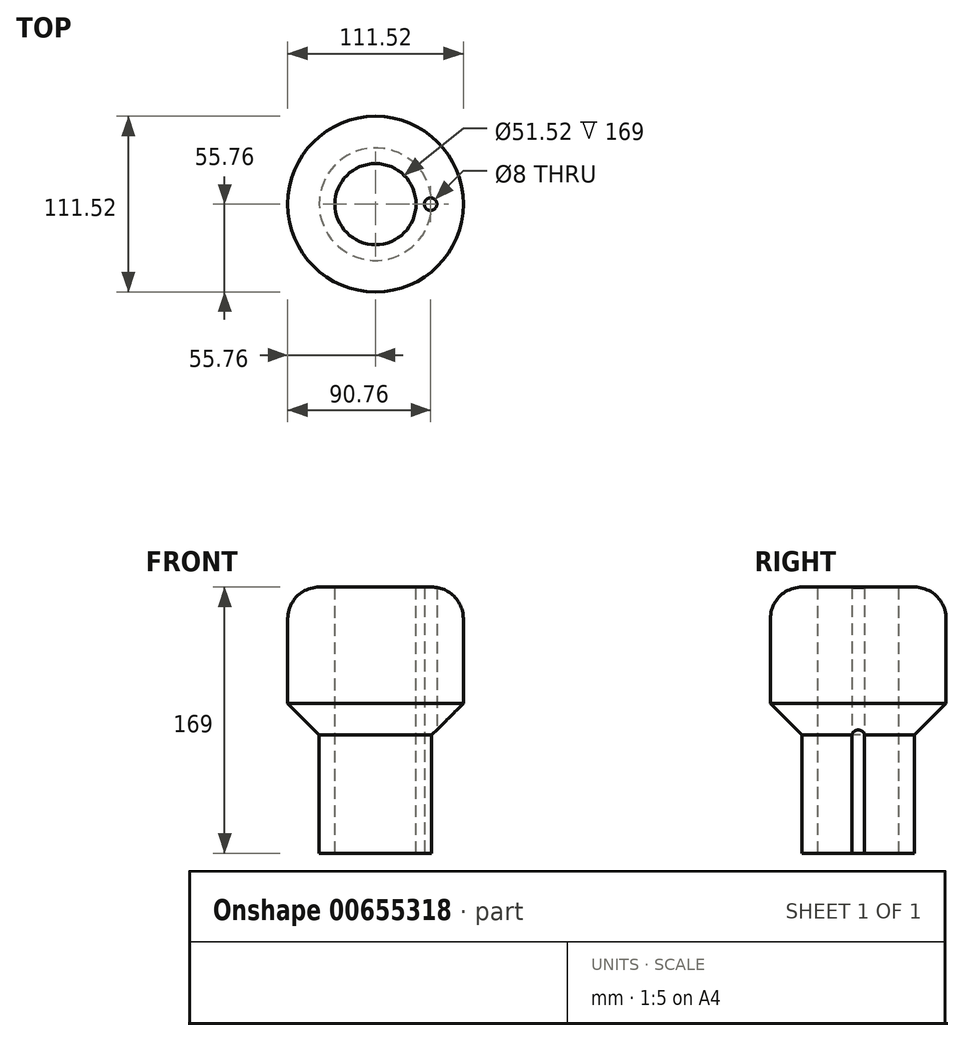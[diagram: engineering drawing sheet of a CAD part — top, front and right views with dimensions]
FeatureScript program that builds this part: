
annotation { "Feature Type Name" : "Feature", "Feature Type Description" : "" }
export const myFeature = defineFeature(function(context is Context, id is Id, definition is map)
    precondition{}
    {
        {
            var Q0;
            Q0=qCreatedBy(makeId("Top.planeOp"),FACE);
            var sketch = newSketch(context, id + "F0", { "sketchPlane" : qUnion([Q0])});
            skCircle(sketch, "E0", {"center": v(0, 0) * mm, "radius": 55.76 * mm});
            skSolve(sketch);
        }
        {
            var Q0;
            Q0=makeQuery(id+"F0.imprint","IMPRINT",FACE,{"disambiguationData":[TD([[makeQuery(id+"F0.imprint","IMPRINT",EDGE,{"derivedFrom":sQuery(id+"F0.wireOp",EDGE,"E0")}),1.0]])]});
            extrude(context, id + "F1", {"entities" : qUnion([Q0]), "depth" : 94 * mm, "offsetDistance" : 25 * mm});
        }
        {
            var Q0;
            Q0=makeQuery(id+"F1.opExtrude","CAP_FACE",FACE,{"disambiguationData":[OSD([sQuery(id+"F0.wireOp",EDGE,"E0")])],"isStart":false});
            var sketch = newSketch(context, id + "F2", { "sketchPlane" : qUnion([Q0])});
            skCircle(sketch, "E1.0", {"center": v(0, 0) * mm, "radius": 25.76 * mm});
            skSolve(sketch);
        }
        {
            var Q0;
            Q0=makeQuery(id+"F2.imprint","IMPRINT",FACE,{"disambiguationData":[TD([[makeQuery(id+"F2.imprint","IMPRINT",EDGE,{"derivedFrom":sQuery(id+"F2.wireOp",EDGE,"E1.0")}),1.0]])]});
            extrude(context, id + "F3", {"entities" : qUnion([Q0]), "operationType" : NewBodyOperationType.REMOVE, "oppositeDirection" : true, "depth" : 179.16 * mm, "offsetDistance" : 25 * mm});
        }
        {
            var Q0;
            Q0=makeQuery(id+"F1.opExtrude","CAP_EDGE",EDGE,{"disambiguationData":[OSD([sQuery(id+"F0.wireOp",EDGE,"E0")])],"isStart":false});
            fillet(context, id + "F4", {"entities" : qUnion([Q0]), "radius" : 20 * mm, "tangentPropagation" : true, "allowEdgeOverflow" : false});
        }
        {
            var Q0;
            Q0=makeQuery(id+"F1.opExtrude","CAP_EDGE",EDGE,{"disambiguationData":[OSD([sQuery(id+"F0.wireOp",EDGE,"E0")])],"isStart":true});
            chamfer(context, id + "F5", {"entities" : qUnion([Q0]), "width" : 20 * mm, "tangentPropagation" : true});
        }
        {
            var Q0;
            Q0=makeQuery(id+"F1.opExtrude","CAP_FACE",FACE,{"disambiguationData":[OSD([sQuery(id+"F0.wireOp",EDGE,"E0")])],"isStart":true});
            var sketch = newSketch(context, id + "F6", { "sketchPlane" : qUnion([Q0])});
            skPoint(sketch, "E2", {"position": v(35, 0) * mm});
            skSolve(sketch);
        }
        {
            var Q0;
            Q0=sQuery(id+"F6.wireOp",VERTEX,"E2");
            var Q1;
            Q1=makeQuery(id+"F1.opExtrude","SWEPT_BODY",BODY,{"disambiguationData":[OSD([sQuery(id+"F0.wireOp",EDGE,"E0")])]});
            hole(context, id + "F7", {"style" : HoleStyle.SIMPLE, "endStyle" : HoleEndStyle.THROUGH, "holeDiameter" : 8 * mm, "majorDiameter" : 5 * mm, "isTappedThrough" : true, "tappedDepth" : 12 * mm, "tapClearance" : 3, "locations" : qUnion([Q0]), "scope" : qUnion([Q1])});
        }
        {
            var Q0;
            Q0=makeQuery(id+"F1.opExtrude","CAP_FACE",FACE,{"disambiguationData":[OSD([sQuery(id+"F0.wireOp",EDGE,"E0")])],"isStart":true});
            extrude(context, id + "F8", {"entities" : qUnion([Q0]), "operationType" : NewBodyOperationType.ADD, "depth" : 75 * mm, "offsetDistance" : 25 * mm});
        }
    });
